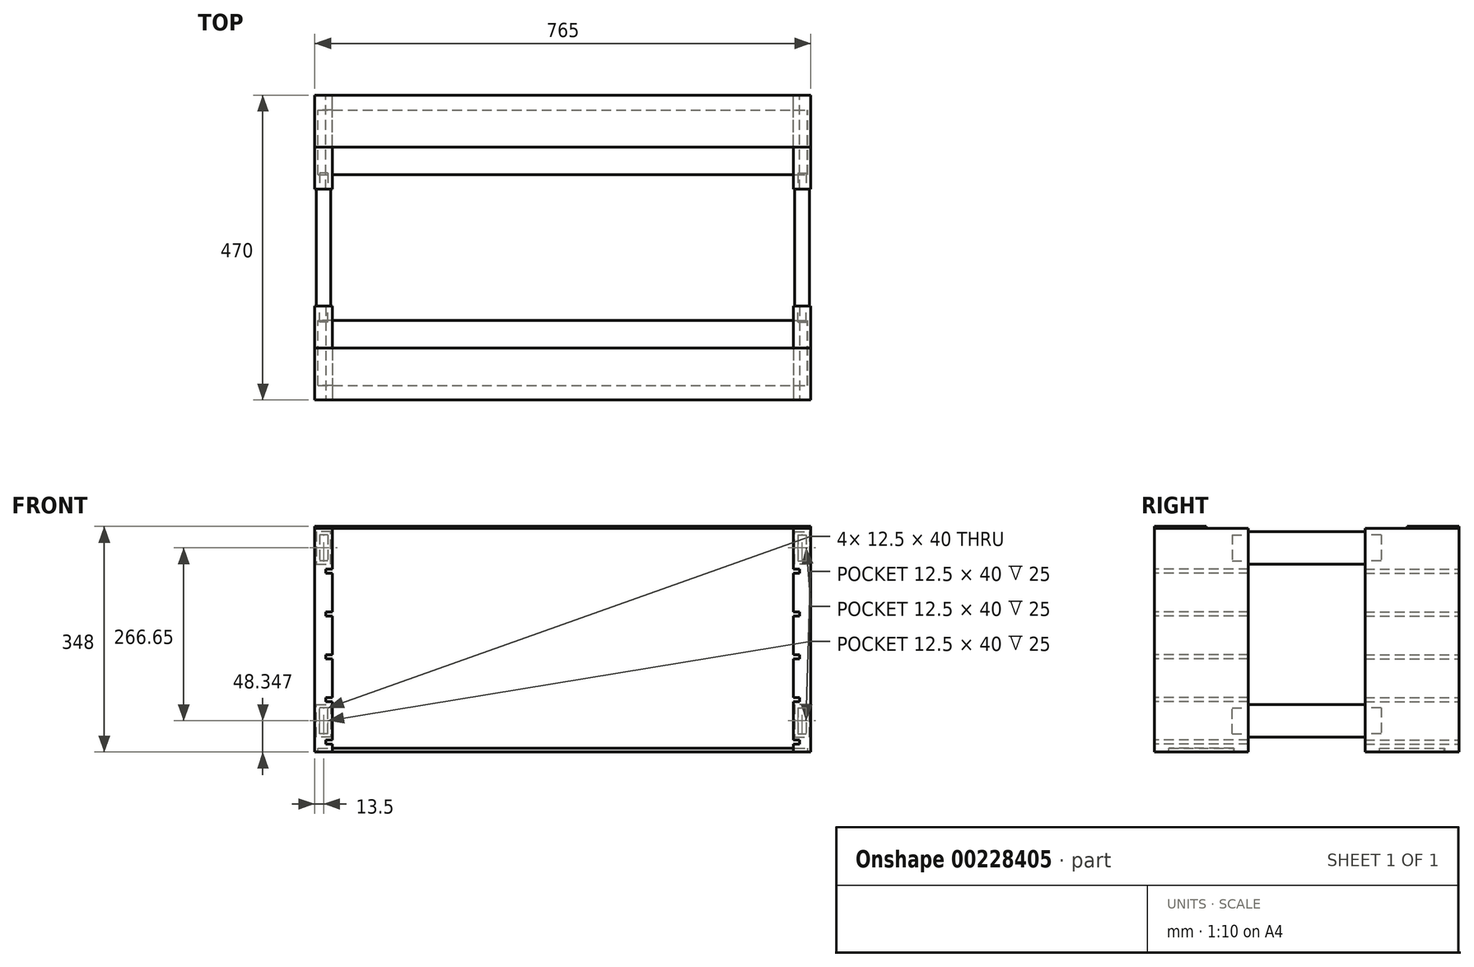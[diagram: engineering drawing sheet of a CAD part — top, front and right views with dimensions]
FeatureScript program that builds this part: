
annotation { "Feature Type Name" : "Feature", "Feature Type Description" : "" }
export const myFeature = defineFeature(function(context is Context, id is Id, definition is map)
    precondition{}
    {
        {
            var Q0;
            Q0=qCreatedBy(makeId("Front.planeOp"),FACE);
            var sketch = newSketch(context, id + "F0", { "sketchPlane" : qUnion([Q0])});
            skLineSegment(sketch, "E0.bottom", {"start": v(0, -43.52) * mm, "end": v(-27, -43.52) * mm});
            skLineSegment(sketch, "E0.top", {"start": v(0, 301.48) * mm, "end": v(-27, 301.48) * mm});
            skLineSegment(sketch, "E0.left", {"start": v(0, -43.52) * mm, "end": v(0, -31.52) * mm});
            skLineSegment(sketch, "E0.right", {"start": v(-27, -43.52) * mm, "end": v(-27, 301.48) * mm});
            skLineSegment(sketch, "E1.bottom", {"start": v(0, -25.17) * mm, "end": v(-10, -25.17) * mm});
            skLineSegment(sketch, "E1.top", {"start": v(0, -31.52) * mm, "end": v(-10, -31.52) * mm});
            skLineSegment(sketch, "E1.right", {"start": v(-10, -25.17) * mm, "end": v(-10, -31.52) * mm});
            skLineSegment(sketch, "E2.bottom", {"start": v(0, 34.48) * mm, "end": v(-10, 34.48) * mm});
            skLineSegment(sketch, "E2.top", {"start": v(0, 40.83) * mm, "end": v(-10, 40.83) * mm});
            skLineSegment(sketch, "E2.right", {"start": v(-10, 34.48) * mm, "end": v(-10, 40.83) * mm});
            skLineSegment(sketch, "E3.0.1.0", {"start": v(0, 100.48) * mm, "end": v(-10, 100.48) * mm});
            skLineSegment(sketch, "E3.0.1.1", {"start": v(-10, 100.48) * mm, "end": v(-10, 106.83) * mm});
            skLineSegment(sketch, "E3.0.1.2", {"start": v(0, 106.83) * mm, "end": v(-10, 106.83) * mm});
            skLineSegment(sketch, "E3.0.2.0", {"start": v(0, 166.48) * mm, "end": v(-10, 166.48) * mm});
            skLineSegment(sketch, "E3.0.2.1", {"start": v(-10, 166.48) * mm, "end": v(-10, 172.83) * mm});
            skLineSegment(sketch, "E3.0.2.2", {"start": v(0, 172.83) * mm, "end": v(-10, 172.83) * mm});
            skLineSegment(sketch, "E3.0.3.0", {"start": v(0, 232.48) * mm, "end": v(-10, 232.48) * mm});
            skLineSegment(sketch, "E3.0.3.1", {"start": v(-10, 232.48) * mm, "end": v(-10, 238.83) * mm});
            skLineSegment(sketch, "E3.0.3.2", {"start": v(0, 238.83) * mm, "end": v(-10, 238.83) * mm});
            skLineSegment(sketch, "E3.direction1", {"start": v(-10, 34.48) * mm, "end": v(15, 34.48) * mm, "construction": true});
            skLineSegment(sketch, "E3.direction2", {"start": v(-10, 34.48) * mm, "end": v(-10, 100.48) * mm, "construction": true});
            skLineSegment(sketch, "E4.trimOffspring", {"start": v(0, 238.83) * mm, "end": v(0, 301.48) * mm});
            skLineSegment(sketch, "E5.trimOffspring", {"start": v(0, 172.83) * mm, "end": v(0, 232.48) * mm});
            skLineSegment(sketch, "E6.trimOffspring", {"start": v(0, 106.83) * mm, "end": v(0, 166.48) * mm});
            skLineSegment(sketch, "E7.trimOffspring", {"start": v(0, 40.83) * mm, "end": v(0, 100.48) * mm});
            skLineSegment(sketch, "E8.trimOffspring", {"start": v(0, -25.17) * mm, "end": v(0, 34.48) * mm});
            skSolve(sketch);
        }
        {
            var Q0;
            Q0 = qSketchRegion(id + "F0", true);
            extrude(context, id + "F1", {"entities" : qUnion([Q0]), "oppositeDirection" : true, "depth" : 145 * mm});
        }
        {
            var Q0;
            Q0=makeQuery(id+"F1.opExtrude","CAP_FACE",FACE,{"disambiguationData":[OSD([sQuery(id+"F0.wireOp",EDGE,"E0.bottom"),sQuery(id+"F0.wireOp",EDGE,"E0.top"),sQuery(id+"F0.wireOp",EDGE,"E0.left"),sQuery(id+"F0.wireOp",EDGE,"E0.right"),sQuery(id+"F0.wireOp",EDGE,"E1.bottom"),sQuery(id+"F0.wireOp",EDGE,"E1.top"),sQuery(id+"F0.wireOp",EDGE,"E1.right"),sQuery(id+"F0.wireOp",EDGE,"E2.bottom"),sQuery(id+"F0.wireOp",EDGE,"E2.top"),sQuery(id+"F0.wireOp",EDGE,"E2.right"),sQuery(id+"F0.wireOp",EDGE,"E3.0.1.0"),sQuery(id+"F0.wireOp",EDGE,"E3.0.1.1"),sQuery(id+"F0.wireOp",EDGE,"E3.0.1.2"),sQuery(id+"F0.wireOp",EDGE,"E3.0.2.0"),sQuery(id+"F0.wireOp",EDGE,"E3.0.2.1"),sQuery(id+"F0.wireOp",EDGE,"E3.0.2.2"),sQuery(id+"F0.wireOp",EDGE,"E3.0.3.0"),sQuery(id+"F0.wireOp",EDGE,"E3.0.3.1"),sQuery(id+"F0.wireOp",EDGE,"E3.0.3.2"),sQuery(id+"F0.wireOp",EDGE,"E4.trimOffspring"),sQuery(id+"F0.wireOp",EDGE,"E5.trimOffspring"),sQuery(id+"F0.wireOp",EDGE,"E6.trimOffspring"),sQuery(id+"F0.wireOp",EDGE,"E7.trimOffspring"),sQuery(id+"F0.wireOp",EDGE,"E8.trimOffspring")])],"isStart":false});
            var sketch = newSketch(context, id + "F2", { "sketchPlane" : qUnion([Q0])});
            skLineSegment(sketch, "E9.bottom", {"start": v(7.25, 291.48) * mm, "end": v(19.75, 291.48) * mm});
            skLineSegment(sketch, "E9.top", {"start": v(7.25, 251.48) * mm, "end": v(19.75, 251.48) * mm});
            skLineSegment(sketch, "E9.left", {"start": v(7.25, 291.48) * mm, "end": v(7.25, 251.48) * mm});
            skLineSegment(sketch, "E9.right", {"start": v(19.75, 291.48) * mm, "end": v(19.75, 251.48) * mm});
            skLineSegment(sketch, "E10.bottom", {"start": v(7.25, 24.83) * mm, "end": v(19.75, 24.83) * mm});
            skLineSegment(sketch, "E10.top", {"start": v(7.25, -15.17) * mm, "end": v(19.75, -15.17) * mm});
            skLineSegment(sketch, "E10.left", {"start": v(7.25, 24.83) * mm, "end": v(7.25, -15.17) * mm});
            skLineSegment(sketch, "E10.right", {"start": v(19.75, 24.83) * mm, "end": v(19.75, -15.17) * mm});
            skSolve(sketch);
        }
        {
            var Q0;
            Q0 = qSketchRegion(id + "F2", true);
            extrude(context, id + "F3", {"entities" : qUnion([Q0]), "operationType" : NewBodyOperationType.REMOVE, "oppositeDirection" : true, "depth" : 25 * mm});
        }
        {
            var Q0;
            Q0=makeQuery(id+"F1.opExtrude","CAP_FACE",FACE,{"disambiguationData":[OSD([sQuery(id+"F0.wireOp",EDGE,"E0.bottom"),sQuery(id+"F0.wireOp",EDGE,"E0.top"),sQuery(id+"F0.wireOp",EDGE,"E0.left"),sQuery(id+"F0.wireOp",EDGE,"E0.right"),sQuery(id+"F0.wireOp",EDGE,"E1.bottom"),sQuery(id+"F0.wireOp",EDGE,"E1.top"),sQuery(id+"F0.wireOp",EDGE,"E1.right"),sQuery(id+"F0.wireOp",EDGE,"E2.bottom"),sQuery(id+"F0.wireOp",EDGE,"E2.top"),sQuery(id+"F0.wireOp",EDGE,"E2.right"),sQuery(id+"F0.wireOp",EDGE,"E3.0.1.0"),sQuery(id+"F0.wireOp",EDGE,"E3.0.1.1"),sQuery(id+"F0.wireOp",EDGE,"E3.0.1.2"),sQuery(id+"F0.wireOp",EDGE,"E3.0.2.0"),sQuery(id+"F0.wireOp",EDGE,"E3.0.2.1"),sQuery(id+"F0.wireOp",EDGE,"E3.0.2.2"),sQuery(id+"F0.wireOp",EDGE,"E3.0.3.0"),sQuery(id+"F0.wireOp",EDGE,"E3.0.3.1"),sQuery(id+"F0.wireOp",EDGE,"E3.0.3.2"),sQuery(id+"F0.wireOp",EDGE,"E4.trimOffspring"),sQuery(id+"F0.wireOp",EDGE,"E5.trimOffspring"),sQuery(id+"F0.wireOp",EDGE,"E6.trimOffspring"),sQuery(id+"F0.wireOp",EDGE,"E7.trimOffspring"),sQuery(id+"F0.wireOp",EDGE,"E8.trimOffspring")])],"isStart":false});
            cPlane(context, id + "F4", {"entities" : qUnion([Q0]), "cplaneType" : CPlaneType.OFFSET, "offset" : 90 * mm, "width" : 150 * mm, "height" : 150 * mm});
        }
        {
            var Q0;
            Q0=makeQuery(id+"F1.opExtrude","SWEPT_FACE",FACE,{"disambiguationData":[OSD([sQuery(id+"F0.wireOp",EDGE,"E4.trimOffspring")])]});
            cPlane(context, id + "F5", {"entities" : qUnion([Q0]), "cplaneType" : CPlaneType.OFFSET, "offset" : 355.5 * mm, "width" : 150 * mm, "height" : 150 * mm});
        }
        {
            var Q0;
            Q0=makeQuery(id+"F1.opExtrude","SWEPT_BODY",BODY,{"disambiguationData":[OSD([sQuery(id+"F0.wireOp",EDGE,"E0.bottom"),sQuery(id+"F0.wireOp",EDGE,"E0.top"),sQuery(id+"F0.wireOp",EDGE,"E0.left"),sQuery(id+"F0.wireOp",EDGE,"E0.right"),sQuery(id+"F0.wireOp",EDGE,"E1.bottom"),sQuery(id+"F0.wireOp",EDGE,"E1.top"),sQuery(id+"F0.wireOp",EDGE,"E1.right"),sQuery(id+"F0.wireOp",EDGE,"E2.bottom"),sQuery(id+"F0.wireOp",EDGE,"E2.top"),sQuery(id+"F0.wireOp",EDGE,"E2.right"),sQuery(id+"F0.wireOp",EDGE,"E3.0.1.0"),sQuery(id+"F0.wireOp",EDGE,"E3.0.1.1"),sQuery(id+"F0.wireOp",EDGE,"E3.0.1.2"),sQuery(id+"F0.wireOp",EDGE,"E3.0.2.0"),sQuery(id+"F0.wireOp",EDGE,"E3.0.2.1"),sQuery(id+"F0.wireOp",EDGE,"E3.0.2.2"),sQuery(id+"F0.wireOp",EDGE,"E3.0.3.0"),sQuery(id+"F0.wireOp",EDGE,"E3.0.3.1"),sQuery(id+"F0.wireOp",EDGE,"E3.0.3.2"),sQuery(id+"F0.wireOp",EDGE,"E4.trimOffspring"),sQuery(id+"F0.wireOp",EDGE,"E5.trimOffspring"),sQuery(id+"F0.wireOp",EDGE,"E6.trimOffspring"),sQuery(id+"F0.wireOp",EDGE,"E7.trimOffspring"),sQuery(id+"F0.wireOp",EDGE,"E8.trimOffspring")])]});
            var Q1;
            Q1=qCreatedBy(id+"F4.planeOp",FACE);
            mirror(context, id + "F6", {"entities" : qUnion([Q0]), "mirrorPlane" : qUnion([Q1])});
        }
        {
            var Q0;
            Q0=makeQuery(id+"F1.opExtrude","SWEPT_BODY",BODY,{"disambiguationData":[OSD([sQuery(id+"F0.wireOp",EDGE,"E0.bottom"),sQuery(id+"F0.wireOp",EDGE,"E0.top"),sQuery(id+"F0.wireOp",EDGE,"E0.left"),sQuery(id+"F0.wireOp",EDGE,"E0.right"),sQuery(id+"F0.wireOp",EDGE,"E1.bottom"),sQuery(id+"F0.wireOp",EDGE,"E1.top"),sQuery(id+"F0.wireOp",EDGE,"E1.right"),sQuery(id+"F0.wireOp",EDGE,"E2.bottom"),sQuery(id+"F0.wireOp",EDGE,"E2.top"),sQuery(id+"F0.wireOp",EDGE,"E2.right"),sQuery(id+"F0.wireOp",EDGE,"E3.0.1.0"),sQuery(id+"F0.wireOp",EDGE,"E3.0.1.1"),sQuery(id+"F0.wireOp",EDGE,"E3.0.1.2"),sQuery(id+"F0.wireOp",EDGE,"E3.0.2.0"),sQuery(id+"F0.wireOp",EDGE,"E3.0.2.1"),sQuery(id+"F0.wireOp",EDGE,"E3.0.2.2"),sQuery(id+"F0.wireOp",EDGE,"E3.0.3.0"),sQuery(id+"F0.wireOp",EDGE,"E3.0.3.1"),sQuery(id+"F0.wireOp",EDGE,"E3.0.3.2"),sQuery(id+"F0.wireOp",EDGE,"E4.trimOffspring"),sQuery(id+"F0.wireOp",EDGE,"E5.trimOffspring"),sQuery(id+"F0.wireOp",EDGE,"E6.trimOffspring"),sQuery(id+"F0.wireOp",EDGE,"E7.trimOffspring"),sQuery(id+"F0.wireOp",EDGE,"E8.trimOffspring")])]});
            var Q1;
            Q1=qCreatedBy(id+"F5.planeOp",FACE);
            mirror(context, id + "F7", {"entities" : qUnion([Q0]), "mirrorPlane" : qUnion([Q1])});
        }
        {
            var Q0;
            Q0=makeQuery(id+"F7.opPattern","COPY",BODY,{"derivedFrom":makeQuery(id+"F1.opExtrude","SWEPT_BODY",BODY,{"disambiguationData":[OSD([sQuery(id+"F0.wireOp",EDGE,"E0.bottom"),sQuery(id+"F0.wireOp",EDGE,"E0.top"),sQuery(id+"F0.wireOp",EDGE,"E0.left"),sQuery(id+"F0.wireOp",EDGE,"E0.right"),sQuery(id+"F0.wireOp",EDGE,"E1.bottom"),sQuery(id+"F0.wireOp",EDGE,"E1.top"),sQuery(id+"F0.wireOp",EDGE,"E1.right"),sQuery(id+"F0.wireOp",EDGE,"E2.bottom"),sQuery(id+"F0.wireOp",EDGE,"E2.top"),sQuery(id+"F0.wireOp",EDGE,"E2.right"),sQuery(id+"F0.wireOp",EDGE,"E3.0.1.0"),sQuery(id+"F0.wireOp",EDGE,"E3.0.1.1"),sQuery(id+"F0.wireOp",EDGE,"E3.0.1.2"),sQuery(id+"F0.wireOp",EDGE,"E3.0.2.0"),sQuery(id+"F0.wireOp",EDGE,"E3.0.2.1"),sQuery(id+"F0.wireOp",EDGE,"E3.0.2.2"),sQuery(id+"F0.wireOp",EDGE,"E3.0.3.0"),sQuery(id+"F0.wireOp",EDGE,"E3.0.3.1"),sQuery(id+"F0.wireOp",EDGE,"E3.0.3.2"),sQuery(id+"F0.wireOp",EDGE,"E4.trimOffspring"),sQuery(id+"F0.wireOp",EDGE,"E5.trimOffspring"),sQuery(id+"F0.wireOp",EDGE,"E6.trimOffspring"),sQuery(id+"F0.wireOp",EDGE,"E7.trimOffspring"),sQuery(id+"F0.wireOp",EDGE,"E8.trimOffspring")])]}),"instanceName":"1"});
            var Q1;
            Q1=qCreatedBy(id+"F4.planeOp",FACE);
            mirror(context, id + "F8", {"entities" : qUnion([Q0]), "mirrorPlane" : qUnion([Q1])});
        }
        {
            var Q0;
            Q0=makeQuery(id+"F6.opPattern","COPY",FACE,{"derivedFrom":makeQuery(id+"F1.opExtrude","CAP_FACE",FACE,{"disambiguationData":[OSD([sQuery(id+"F0.wireOp",EDGE,"E0.bottom"),sQuery(id+"F0.wireOp",EDGE,"E0.top"),sQuery(id+"F0.wireOp",EDGE,"E0.left"),sQuery(id+"F0.wireOp",EDGE,"E0.right"),sQuery(id+"F0.wireOp",EDGE,"E1.bottom"),sQuery(id+"F0.wireOp",EDGE,"E1.top"),sQuery(id+"F0.wireOp",EDGE,"E1.right"),sQuery(id+"F0.wireOp",EDGE,"E2.bottom"),sQuery(id+"F0.wireOp",EDGE,"E2.top"),sQuery(id+"F0.wireOp",EDGE,"E2.right"),sQuery(id+"F0.wireOp",EDGE,"E3.0.1.0"),sQuery(id+"F0.wireOp",EDGE,"E3.0.1.1"),sQuery(id+"F0.wireOp",EDGE,"E3.0.1.2"),sQuery(id+"F0.wireOp",EDGE,"E3.0.2.0"),sQuery(id+"F0.wireOp",EDGE,"E3.0.2.1"),sQuery(id+"F0.wireOp",EDGE,"E3.0.2.2"),sQuery(id+"F0.wireOp",EDGE,"E3.0.3.0"),sQuery(id+"F0.wireOp",EDGE,"E3.0.3.1"),sQuery(id+"F0.wireOp",EDGE,"E3.0.3.2"),sQuery(id+"F0.wireOp",EDGE,"E4.trimOffspring"),sQuery(id+"F0.wireOp",EDGE,"E5.trimOffspring"),sQuery(id+"F0.wireOp",EDGE,"E6.trimOffspring"),sQuery(id+"F0.wireOp",EDGE,"E7.trimOffspring"),sQuery(id+"F0.wireOp",EDGE,"E8.trimOffspring")])],"isStart":false}),"instanceName":"1"});
            var sketch = newSketch(context, id + "F9", { "sketchPlane" : qUnion([Q0])});
            skLineSegment(sketch, "E11.bottom", {"start": v(-19.75, 291.48) * mm, "end": v(-7.25, 291.48) * mm});
            skLineSegment(sketch, "E11.top", {"start": v(-19.75, 251.48) * mm, "end": v(-7.25, 251.48) * mm});
            skLineSegment(sketch, "E11.left", {"start": v(-19.75, 291.48) * mm, "end": v(-19.75, 251.48) * mm});
            skLineSegment(sketch, "E11.right", {"start": v(-7.25, 291.48) * mm, "end": v(-7.25, 251.48) * mm});
            skSolve(sketch);
        }
        {
            var Q0;
            Q0 = qSketchRegion(id + "F9", true);
            extrude(context, id + "F10", {"entities" : qUnion([Q0]), "oppositeDirection" : true, "depth" : 25 * mm});
        }
        {
            var Q0;
            Q0=makeQuery(id+"F6.opPattern","COPY",FACE,{"derivedFrom":makeQuery(id+"F1.opExtrude","CAP_FACE",FACE,{"disambiguationData":[OSD([sQuery(id+"F0.wireOp",EDGE,"E0.bottom"),sQuery(id+"F0.wireOp",EDGE,"E0.top"),sQuery(id+"F0.wireOp",EDGE,"E0.left"),sQuery(id+"F0.wireOp",EDGE,"E0.right"),sQuery(id+"F0.wireOp",EDGE,"E1.bottom"),sQuery(id+"F0.wireOp",EDGE,"E1.top"),sQuery(id+"F0.wireOp",EDGE,"E1.right"),sQuery(id+"F0.wireOp",EDGE,"E2.bottom"),sQuery(id+"F0.wireOp",EDGE,"E2.top"),sQuery(id+"F0.wireOp",EDGE,"E2.right"),sQuery(id+"F0.wireOp",EDGE,"E3.0.1.0"),sQuery(id+"F0.wireOp",EDGE,"E3.0.1.1"),sQuery(id+"F0.wireOp",EDGE,"E3.0.1.2"),sQuery(id+"F0.wireOp",EDGE,"E3.0.2.0"),sQuery(id+"F0.wireOp",EDGE,"E3.0.2.1"),sQuery(id+"F0.wireOp",EDGE,"E3.0.2.2"),sQuery(id+"F0.wireOp",EDGE,"E3.0.3.0"),sQuery(id+"F0.wireOp",EDGE,"E3.0.3.1"),sQuery(id+"F0.wireOp",EDGE,"E3.0.3.2"),sQuery(id+"F0.wireOp",EDGE,"E4.trimOffspring"),sQuery(id+"F0.wireOp",EDGE,"E5.trimOffspring"),sQuery(id+"F0.wireOp",EDGE,"E6.trimOffspring"),sQuery(id+"F0.wireOp",EDGE,"E7.trimOffspring"),sQuery(id+"F0.wireOp",EDGE,"E8.trimOffspring")])],"isStart":false}),"instanceName":"1"});
            var sketch = newSketch(context, id + "F11", { "sketchPlane" : qUnion([Q0])});
            skLineSegment(sketch, "E12.0", {"start": v(-24.75, 246.48) * mm, "end": v(-2.25, 246.48) * mm});
            skLineSegment(sketch, "E12.1", {"start": v(-24.75, 296.48) * mm, "end": v(-24.75, 246.48) * mm});
            skLineSegment(sketch, "E12.2", {"start": v(-2.25, 296.48) * mm, "end": v(-24.75, 296.48) * mm});
            skLineSegment(sketch, "E12.3", {"start": v(-2.25, 246.48) * mm, "end": v(-2.25, 296.48) * mm});
            skSolve(sketch);
        }
        {
            var Q0;
            Q0 = qSketchRegion(id + "F11", true);
            extrude(context, id + "F12", {"entities" : qUnion([Q0]), "endBound" : BoundingType.UP_TO_NEXT, "depth" : 25 * mm});
        }
        {
            var Q0;
            Q0=makeQuery(id+"F12.opExtrude","SWEPT_BODY",BODY,{"disambiguationData":[OSD([sQuery(id+"F11.wireOp",EDGE,"E12.0"),sQuery(id+"F11.wireOp",EDGE,"E12.1"),sQuery(id+"F11.wireOp",EDGE,"E12.2"),sQuery(id+"F11.wireOp",EDGE,"E12.3")])]});
            var Q1;
            Q1=qCreatedBy(id+"F5.planeOp",FACE);
            mirror(context, id + "F13", {"entities" : qUnion([Q0]), "mirrorPlane" : qUnion([Q1])});
        }
        {
            var Q0;
            Q0=makeQuery(id+"F12.opExtrude","SWEPT_FACE",FACE,{"disambiguationData":[OSD([sQuery(id+"F11.wireOp",EDGE,"E12.0")])]});
            cPlane(context, id + "F14", {"entities" : qUnion([Q0]), "cplaneType" : CPlaneType.OFFSET, "offset" : 108.33 * mm, "width" : 150 * mm, "height" : 150 * mm});
        }
        {
            var Q0;
            Q0=makeQuery(id+"F12.opExtrude","SWEPT_BODY",BODY,{"disambiguationData":[OSD([sQuery(id+"F11.wireOp",EDGE,"E12.0"),sQuery(id+"F11.wireOp",EDGE,"E12.1"),sQuery(id+"F11.wireOp",EDGE,"E12.2"),sQuery(id+"F11.wireOp",EDGE,"E12.3")])]});
            var Q1;
            Q1=qCreatedBy(id+"F14.planeOp",FACE);
            mirror(context, id + "F15", {"entities" : qUnion([Q0]), "mirrorPlane" : qUnion([Q1])});
        }
        {
            var Q0;
            Q0=makeQuery(id+"F13.opPattern","COPY",BODY,{"derivedFrom":makeQuery(id+"F12.opExtrude","SWEPT_BODY",BODY,{"disambiguationData":[OSD([sQuery(id+"F11.wireOp",EDGE,"E12.0"),sQuery(id+"F11.wireOp",EDGE,"E12.1"),sQuery(id+"F11.wireOp",EDGE,"E12.2"),sQuery(id+"F11.wireOp",EDGE,"E12.3")])]}),"instanceName":"1"});
            var Q1;
            Q1=qCreatedBy(id+"F14.planeOp",FACE);
            mirror(context, id + "F16", {"entities" : qUnion([Q0]), "mirrorPlane" : qUnion([Q1])});
        }
        {
            var Q0;
            Q0=makeQuery(id+"F6.opPattern","COPY",FACE,{"derivedFrom":makeQuery(id+"F1.opExtrude","SWEPT_FACE",FACE,{"disambiguationData":[OSD([sQuery(id+"F0.wireOp",EDGE,"E0.bottom")])]}),"instanceName":"1"});
            var sketch = newSketch(context, id + "F17", { "sketchPlane" : qUnion([Q0])});
            skLineSegment(sketch, "E13.bottom", {"start": v(0, -347.5) * mm, "end": v(-22, -347.5) * mm});
            skLineSegment(sketch, "E13.top", {"start": v(0, -447.5) * mm, "end": v(-22, -447.5) * mm});
            skLineSegment(sketch, "E13.left", {"start": v(0, -347.5) * mm, "end": v(0, -447.5) * mm});
            skLineSegment(sketch, "E13.right", {"start": v(-22, -347.5) * mm, "end": v(-22, -447.5) * mm});
            skSolve(sketch);
        }
        {
            var Q0;
            Q0 = qSketchRegion(id + "F17", true);
            extrude(context, id + "F18", {"entities" : qUnion([Q0]), "operationType" : NewBodyOperationType.REMOVE, "oppositeDirection" : true, "depth" : 6 * mm});
        }
        {
            var Q0;
            Q0=makeQuery(id+"F1.opExtrude","SWEPT_FACE",FACE,{"disambiguationData":[OSD([sQuery(id+"F0.wireOp",EDGE,"E0.bottom")])]});
            var sketch = newSketch(context, id + "F19", { "sketchPlane" : qUnion([Q0])});
            skLineSegment(sketch, "E14.bottom", {"start": v(0, -22.5) * mm, "end": v(-22, -22.5) * mm});
            skLineSegment(sketch, "E14.top", {"start": v(0, -122.5) * mm, "end": v(-22, -122.5) * mm});
            skLineSegment(sketch, "E14.left", {"start": v(0, -22.5) * mm, "end": v(0, -122.5) * mm});
            skLineSegment(sketch, "E14.right", {"start": v(-22, -22.5) * mm, "end": v(-22, -122.5) * mm});
            skSolve(sketch);
        }
        {
            var Q0;
            Q0 = qSketchRegion(id + "F19", true);
            extrude(context, id + "F20", {"entities" : qUnion([Q0]), "operationType" : NewBodyOperationType.REMOVE, "oppositeDirection" : true, "depth" : 6 * mm});
        }
        {
            var Q0;
            Q0=makeQuery(id+"F7.opPattern","COPY",FACE,{"derivedFrom":makeQuery(id+"F1.opExtrude","SWEPT_FACE",FACE,{"disambiguationData":[OSD([sQuery(id+"F0.wireOp",EDGE,"E0.bottom")])]}),"instanceName":"1"});
            var sketch = newSketch(context, id + "F21", { "sketchPlane" : qUnion([Q0])});
            skLineSegment(sketch, "E15.bottom", {"start": v(711, -22.5) * mm, "end": v(733, -22.5) * mm});
            skLineSegment(sketch, "E15.top", {"start": v(711, -122.5) * mm, "end": v(733, -122.5) * mm});
            skLineSegment(sketch, "E15.left", {"start": v(711, -22.5) * mm, "end": v(711, -122.5) * mm});
            skLineSegment(sketch, "E15.right", {"start": v(733, -22.5) * mm, "end": v(733, -122.5) * mm});
            skSolve(sketch);
        }
        {
            var Q0;
            Q0 = qSketchRegion(id + "F21", true);
            extrude(context, id + "F22", {"entities" : qUnion([Q0]), "operationType" : NewBodyOperationType.REMOVE, "oppositeDirection" : true, "depth" : 6 * mm});
        }
        {
            var Q0;
            Q0=makeQuery(id+"F8.opPattern","COPY",FACE,{"derivedFrom":makeQuery(id+"F7.opPattern","COPY",FACE,{"derivedFrom":makeQuery(id+"F1.opExtrude","SWEPT_FACE",FACE,{"disambiguationData":[OSD([sQuery(id+"F0.wireOp",EDGE,"E0.bottom")])]}),"instanceName":"1"}),"instanceName":"1"});
            var sketch = newSketch(context, id + "F23", { "sketchPlane" : qUnion([Q0])});
            skLineSegment(sketch, "E16.bottom", {"start": v(711, -347.5) * mm, "end": v(733, -347.5) * mm});
            skLineSegment(sketch, "E16.top", {"start": v(711, -447.5) * mm, "end": v(733, -447.5) * mm});
            skLineSegment(sketch, "E16.left", {"start": v(711, -347.5) * mm, "end": v(711, -447.5) * mm});
            skLineSegment(sketch, "E16.right", {"start": v(733, -347.5) * mm, "end": v(733, -447.5) * mm});
            skSolve(sketch);
        }
        {
            var Q0;
            Q0 = qSketchRegion(id + "F23", true);
            extrude(context, id + "F24", {"entities" : qUnion([Q0]), "operationType" : NewBodyOperationType.REMOVE, "oppositeDirection" : true, "depth" : 6 * mm});
        }
        {
            var Q0;
            Q0=makeQuery(id+"F18.boolean.opBoolean","COPY",FACE,{"derivedFrom":makeQuery(id+"F18.opExtrude","CAP_FACE",FACE,{"disambiguationData":[OSD([sQuery(id+"F17.wireOp",EDGE,"E13.bottom"),sQuery(id+"F17.wireOp",EDGE,"E13.top"),sQuery(id+"F17.wireOp",EDGE,"E13.left"),sQuery(id+"F17.wireOp",EDGE,"E13.right")])],"isStart":false})});
            var sketch = newSketch(context, id + "F25", { "sketchPlane" : qUnion([Q0])});
            skLineSegment(sketch, "E17.bottom", {"start": v(-22, -347.5) * mm, "end": v(733.38, -347.5) * mm});
            skLineSegment(sketch, "E17.top", {"start": v(-22, -447.21) * mm, "end": v(733.38, -447.21) * mm});
            skLineSegment(sketch, "E17.left", {"start": v(-22, -347.5) * mm, "end": v(-22, -447.21) * mm});
            skLineSegment(sketch, "E17.right", {"start": v(733.38, -347.5) * mm, "end": v(733.38, -447.21) * mm});
            skSolve(sketch);
        }
        {
            var Q0;
            Q0 = qSketchRegion(id + "F25", true);
            extrude(context, id + "F26", {"entities" : qUnion([Q0]), "depth" : 6 * mm});
        }
        {
            var Q0;
            Q0=makeQuery(id+"F20.boolean.opBoolean","COPY",FACE,{"derivedFrom":makeQuery(id+"F20.opExtrude","CAP_FACE",FACE,{"disambiguationData":[OSD([sQuery(id+"F19.wireOp",EDGE,"E14.bottom"),sQuery(id+"F19.wireOp",EDGE,"E14.top"),sQuery(id+"F19.wireOp",EDGE,"E14.left"),sQuery(id+"F19.wireOp",EDGE,"E14.right")])],"isStart":false})});
            var sketch = newSketch(context, id + "F27", { "sketchPlane" : qUnion([Q0])});
            skLineSegment(sketch, "E18.bottom", {"start": v(-22, -22.5) * mm, "end": v(733.14, -22.5) * mm});
            skLineSegment(sketch, "E18.top", {"start": v(-22, -122.58) * mm, "end": v(733.14, -122.58) * mm});
            skLineSegment(sketch, "E18.left", {"start": v(-22, -22.5) * mm, "end": v(-22, -122.58) * mm});
            skLineSegment(sketch, "E18.right", {"start": v(733.14, -22.5) * mm, "end": v(733.14, -122.58) * mm});
            skSolve(sketch);
        }
        {
            var Q0;
            Q0 = qSketchRegion(id + "F27", true);
            extrude(context, id + "F28", {"entities" : qUnion([Q0]), "depth" : 6 * mm});
        }
        {
            var Q0;
            Q0=makeQuery(id+"F6.opPattern","COPY",FACE,{"derivedFrom":makeQuery(id+"F1.opExtrude","SWEPT_FACE",FACE,{"disambiguationData":[OSD([sQuery(id+"F0.wireOp",EDGE,"E0.top")])]}),"instanceName":"1"});
            var sketch = newSketch(context, id + "F29", { "sketchPlane" : qUnion([Q0])});
            skLineSegment(sketch, "E19.bottom", {"start": v(-27, 470) * mm, "end": v(738, 470) * mm});
            skLineSegment(sketch, "E19.top", {"start": v(-27, 390) * mm, "end": v(738, 390) * mm});
            skLineSegment(sketch, "E19.left", {"start": v(-27, 470) * mm, "end": v(-27, 390) * mm});
            skLineSegment(sketch, "E19.right", {"start": v(738, 470) * mm, "end": v(738, 390) * mm});
            skSolve(sketch);
        }
        {
            var Q0;
            Q0 = qSketchRegion(id + "F29", true);
            extrude(context, id + "F30", {"entities" : qUnion([Q0]), "depth" : 3 * mm});
        }
        {
            var Q0;
            Q0=makeQuery(id+"F30.opExtrude","SWEPT_BODY",BODY,{"disambiguationData":[OSD([sQuery(id+"F29.wireOp",EDGE,"E19.bottom"),sQuery(id+"F29.wireOp",EDGE,"E19.top"),sQuery(id+"F29.wireOp",EDGE,"E19.left"),sQuery(id+"F29.wireOp",EDGE,"E19.right")])]});
            var Q1;
            Q1=qCreatedBy(id+"F4.planeOp",FACE);
            mirror(context, id + "F31", {"entities" : qUnion([Q0]), "mirrorPlane" : qUnion([Q1])});
        }
        {
            var Q0;
            Q0=makeQuery(id+"F9.imprint","IMPRINT",FACE,{"disambiguationData":[TD([[makeQuery(id+"F9.imprint","IMPRINT",EDGE,{"derivedFrom":sQuery(id+"F9.wireOp",EDGE,"E11.bottom")}),1.0]])]});
            extrude(context, id + "F32", {"entities" : qUnion([Q0]), "operationType" : NewBodyOperationType.ADD, "oppositeDirection" : true, "depth" : 25 * mm});
        }
    });
